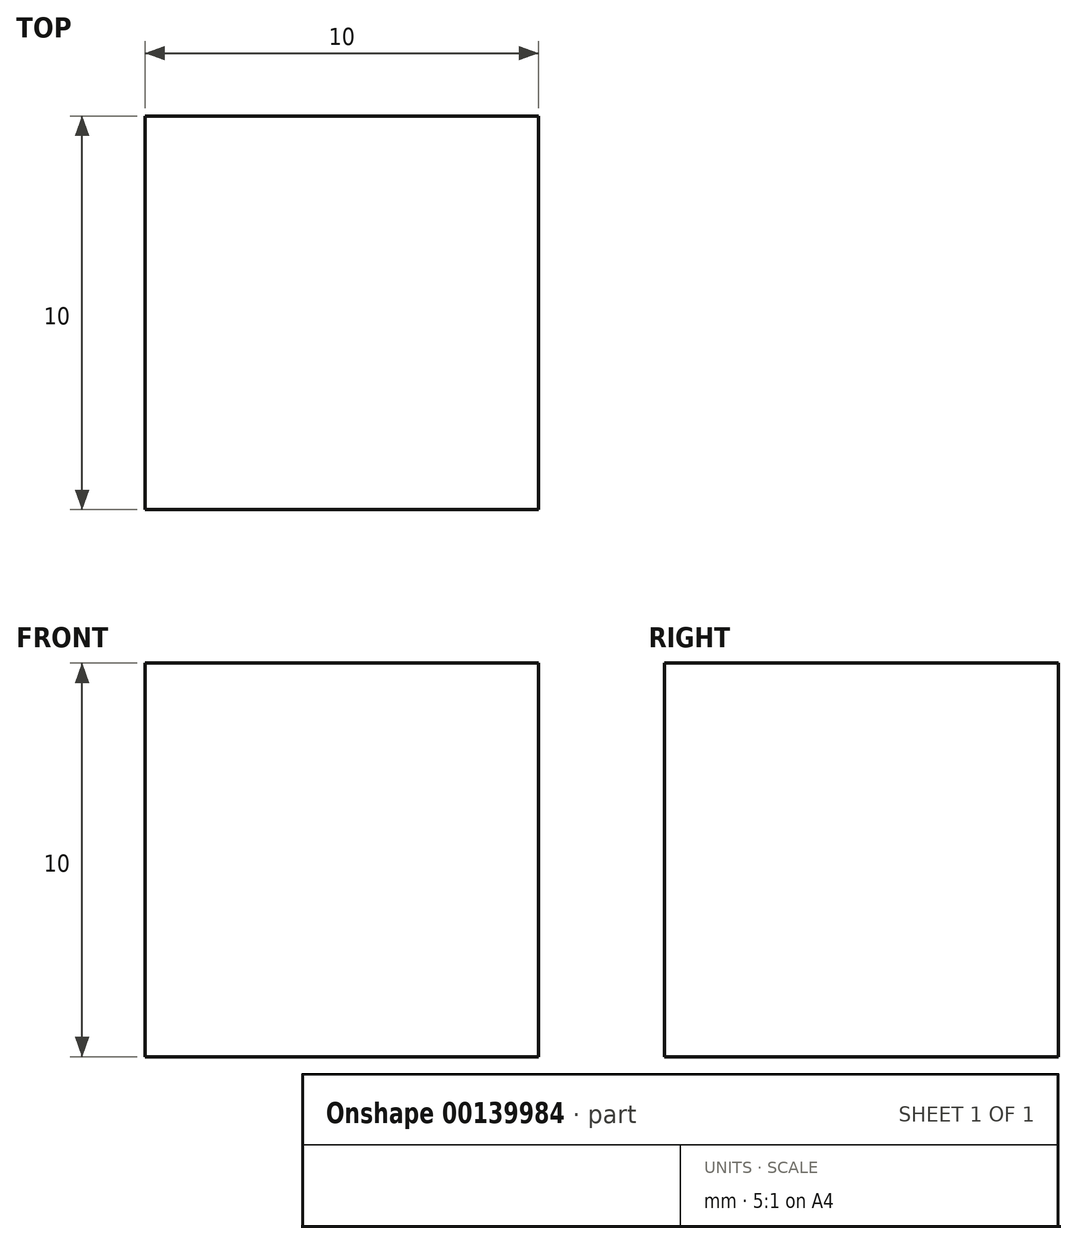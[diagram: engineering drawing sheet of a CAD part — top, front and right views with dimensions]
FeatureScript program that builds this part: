
annotation { "Feature Type Name" : "Feature", "Feature Type Description" : "" }
export const myFeature = defineFeature(function(context is Context, id is Id, definition is map)
    precondition{}
    {
        {
            var Q0;
            Q0=qCreatedBy(makeId("Top.planeOp"),FACE);
            var sketch = newSketch(context, id + "F0", { "sketchPlane" : qUnion([Q0])});
            skLineSegment(sketch, "E0.bottom", {"start": v(5, 5) * mm, "end": v(-5, 5) * mm});
            skLineSegment(sketch, "E0.top", {"start": v(5, -5) * mm, "end": v(-5, -5) * mm});
            skLineSegment(sketch, "E0.left", {"start": v(5, 5) * mm, "end": v(5, -5) * mm});
            skLineSegment(sketch, "E0.right", {"start": v(-5, 5) * mm, "end": v(-5, -5) * mm});
            skPoint(sketch, "E0.middle", {"position": v(0, 0) * mm});
            skSolve(sketch);
        }
        {
            var Q0;
            Q0 = qSketchRegion(id + "F0", true);
            extrude(context, id + "F1", {"entities" : qUnion([Q0]), "depth" : 10 * mm});
        }
    });
